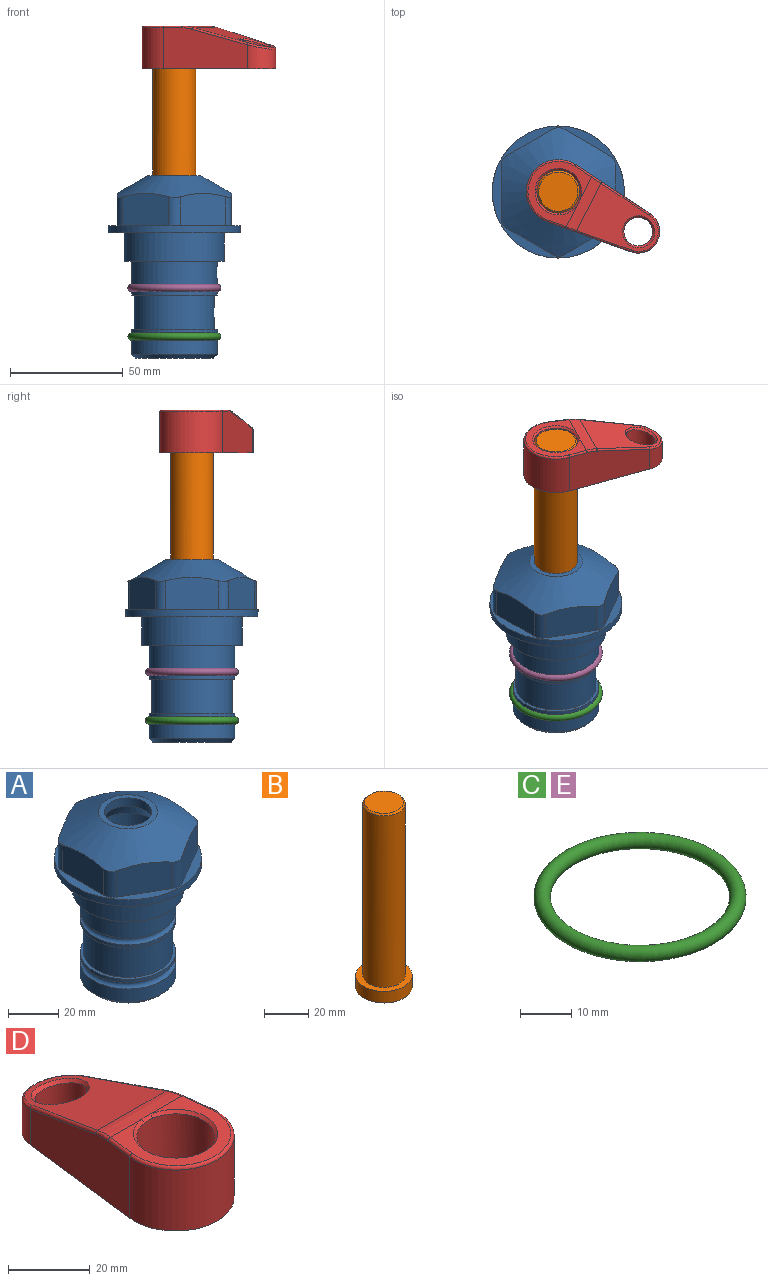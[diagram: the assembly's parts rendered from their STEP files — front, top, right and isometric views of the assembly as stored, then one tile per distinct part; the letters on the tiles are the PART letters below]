
ASSEMBLY  parts=5 mates=4
PART A: 36 faces, bbox 58.7x58.7x81 mm
  f0: cylinder r=17.78mm len=35.56mm, axis (0,0,1), area 1670.8mm2, adj f23,f24,f31
  f1: cylinder r=19.05mm len=38.1mm, axis (0,0,1), area 1191.9mm2, adj f26,f27,f30
  f2: plane 58.66x58.66mm, normal (0,0,-1), area 1150.6mm2, adj f3,f28
  f3: cylinder r=29.33mm len=58.66mm, axis (0,0,-1), area 585.1mm2, adj f2,f4
  f4: plane 58.66x58.66mm, normal (0,0,1), area 475.9mm2, adj f3,f5,f6,f7,f8,f9,f10,f11
  f5: plane 20.32x14.34mm, normal (-0.5,0.87,0), area 324.4mm2, adj f4,f15,f16,f17
  f6: plane 20.32x14.34mm, normal (0.5,0.87,0), area 324.4mm2, adj f4,f14,f15,f17
  f7: plane 23.48x14.34mm, normal (1,0,0), area 324.4mm2, adj f4,f13,f14,f17
  f8: plane 20.32x14.34mm, normal (0.5,-0.87,0), area 324.4mm2, adj f4,f12,f13,f17
  f9: plane 20.32x14.34mm, normal (-0.5,-0.87,0), area 324.4mm2, adj f4,f11,f12,f17
  f10: plane 23.48x14.34mm, normal (-1,0,0), area 324.4mm2, adj f4,f11,f16,f17
  f11: cylinder r=5.08mm len=12.85mm, axis (0,0,-1), area 67.2mm2, adj f4,f9,f10,f17
  f12: cylinder r=5.08mm len=12.85mm, axis (0,0,-1), area 67.2mm2, adj f4,f8,f9,f17
  f13: cylinder r=5.08mm len=12.85mm, axis (0,0,-1), area 67.2mm2, adj f4,f7,f8,f17
  f14: cylinder r=5.08mm len=12.85mm, axis (0,0,-1), area 67.2mm2, adj f4,f6,f7,f17
  f15: cylinder r=5.08mm len=12.85mm, axis (0,0,-1), area 67.2mm2, adj f4,f5,f6,f17
  f16: cylinder r=5.08mm len=12.85mm, axis (0,0,-1), area 67.2mm2, adj f4,f5,f10,f17
  f17: cone r=11.73mm half-angle=60deg, axis (0,0,-1), area 2071.8mm2, adj f5,f6,f7,f8,f9,f10,f11,f12
  f18: plane 23.46x23.46mm, normal (0,0,1), area 147.4mm2, adj f17,f35
  f19: plane 34.93x34.93mm, normal (0,0,-1), area 958mm2, adj f29
  f20: cylinder r=19.05mm len=38.1mm, axis (0,0,1), area 760.1mm2, adj f21,f29
  f21: torus R=19.05mm, axis (0,0,1), area 565.3mm2, adj f20,f22
  f22: cylinder r=19.05mm len=38.1mm, axis (0,0,1), area 190mm2, adj f21,f23
  f23: plane 38.1x38.1mm, normal (0,0,1), area 146.9mm2, adj f0,f22
  f24: plane 38.1x38.1mm, normal (0,0,-1), area 146.9mm2, adj f0,f25
  f25: cylinder r=19.05mm len=38.1mm, axis (0,0,1), area 190mm2, adj f24,f26
  f26: torus R=19.05mm, axis (0,0,1), area 565.3mm2, adj f1,f25
  f27: plane 44.45x44.45mm, normal (0,0,-1), area 411.7mm2, adj f1,f28
  f28: cylinder r=22.23mm len=44.45mm, axis (0,0,1), area 1773.5mm2, adj f2,f27
  f29: cone r=19.05mm half-angle=45deg, axis (0,0,1), area 257.5mm2, adj f19,f20
  f30: cylinder r=3.17mm len=6.75mm, axis (-1,0,0), area 128mm2, adj f1,f33
  f31: cylinder r=3.17mm len=6.35mm, axis (-1,0,0), area 102.5mm2, adj f0,f33
  f32: plane 25.4x25.4mm, normal (0,0,1), area 506.7mm2, adj f33
  f33: cylinder r=12.7mm len=66.42mm, axis (0,0,-1), area 5236.2mm2, adj f30,f31,f32,f34
  f34: cone r=9.53mm half-angle=30deg, axis (0,0,-1), area 443.4mm2, adj f33,f35
  f35: cylinder r=9.53mm len=19.05mm, axis (0,0,-1), area 240.9mm2, adj f18,f34
PART B: 6 faces, bbox 25.4x25.4x101.6 mm
  f0: plane 17.46x17.46mm, normal (0,0,1), area 239.5mm2, adj f5
  f1: plane 25.4x25.4mm, normal (0,0,-1), area 506.7mm2, adj f2
  f2: cylinder r=12.7mm len=25.4mm, axis (0,0,1), area 506.7mm2, adj f1,f3
  f3: plane 25.4x25.4mm, normal (0,0,1), area 221.7mm2, adj f2,f4
  f4: cylinder r=9.53mm len=94.46mm, axis (0,0,1), area 5653mm2, adj f3,f5
  f5: cone r=8.73mm half-angle=45deg, axis (0,0,-1), area 64.4mm2, adj f0,f4
PART C: 1 faces, bbox 44.7x44.7x3.2 mm
  f0: torus R=19.05mm, axis (0,0,1), area 1193.9mm2
PART D: 31 faces, bbox 31.7x65.5x19.8 mm
  f0: plane 39.12x18.26mm, normal (0.99,0.12,0), area 612.2mm2, adj f1,f4,f7,f11,f13,f15
  f1: cylinder r=9.53mm len=18.91mm, axis (0,0,-1), area 296.1mm2, adj f0,f2,f7,f17
  f2: plane 39.12x18.26mm, normal (-0.99,0.12,0), area 612.2mm2, adj f1,f4,f7,f12,f14,f16
  f3: cylinder r=6.35mm len=12.7mm, axis (0,0,-1), area 362.4mm2, adj f7,f18
  f4: cylinder r=14.29mm len=28.58mm, axis (0,0,-1), area 882.2mm2, adj f0,f2,f7,f10
  f5: cylinder r=9.53mm len=19.05mm, axis (0,0,-1), area 1092.6mm2, adj f7,f19,f20
  f6: plane 26.99x23.69mm, normal (0,0,1), area 216.2mm2, adj f9,f10,f11,f12,f19
  f7: plane 63.5x28.58mm, normal (0,0,-1), area 661.8mm2, adj f0,f1,f2,f3,f4,f5,f22,f23
  f8: plane 33.52x23.6mm, normal (0,0.26,0.97), area 486mm2, adj f9,f15,f16,f17,f18
  f9: cylinder r=19.05mm len=24.72mm, axis (1,0,0), area 120.4mm2, adj f6,f8,f13,f14,f20
  f10: torus R=13.49mm, axis (0,0,1), area 59mm2, adj f4,f6,f11,f12
  f11: cylinder r=0.79mm len=8.67mm, axis (0.12,-0.99,0), area 10.8mm2, adj f0,f6,f10,f13
  f12: cylinder r=0.79mm len=8.67mm, axis (0.12,0.99,0), area 10.8mm2, adj f2,f6,f10,f14
  f13: bspline ~4.95x1.42mm, area 6.1mm2, adj f0,f9,f11,f15
  f14: bspline ~4.95x1.42mm, area 6.1mm2, adj f2,f9,f12,f16
  f15: cylinder r=0.79mm len=25.95mm, axis (0.12,-0.96,0.26), area 32.9mm2, adj f0,f8,f13,f17
  f16: cylinder r=0.79mm len=25.95mm, axis (0.12,0.96,-0.26), area 32.9mm2, adj f2,f8,f14,f17
  f17: bspline ~18.91x8.38mm, area 30mm2, adj f1,f8,f15,f16
  f18: bspline ~14.29x14.29mm, area 48.3mm2, adj f3,f8
  f19: cone r=9.53mm half-angle=45deg, axis (0,0,1), area 66.5mm2, adj f5,f6,f20
  f20: bspline ~3.22x0.96mm, area 3.5mm2, adj f5,f9,f19
  f21: plane 2.75x2.72mm, normal (0,0,-1), area 2.9mm2, adj f23,f25,f28
  f22: plane 23.05x15.88mm, normal (-0.99,-0.12,0), area 323.6mm2, adj f7,f25,f26,f27,f28,f29
  f23: plane 23.05x15.88mm, normal (0.99,-0.12,0), area 323.6mm2, adj f7,f21,f25,f27,f28,f30
  f24: cylinder r=9.53mm len=10.69mm, axis (0,0,-1), area 114.7mm2, adj f7,f27,f29,f30
  f25: cylinder r=12.7mm len=20.59mm, axis (0,0,-1), area 381.1mm2, adj f7,f21,f22,f23,f26,f28
  f26: plane 2.75x2.72mm, normal (0,0,-1), area 2.9mm2, adj f22,f25,f28
  f27: plane 19.72x18.37mm, normal (0,-0.26,-0.97), area 291.8mm2, adj f22,f23,f24,f28,f29,f30
  f28: cylinder r=15.88mm len=19.92mm, axis (1,0,0), area 54.8mm2, adj f21,f22,f23,f25,f26,f27
  f29: cylinder r=1.59mm len=11mm, axis (0,0,-1), area 34.7mm2, adj f7,f22,f24,f27
  f30: cylinder r=1.59mm len=11mm, axis (0,0,-1), area 34.7mm2, adj f7,f23,f24,f27
PART E: same geometry as C
PLACE A at identity fixed
PLACE B rot(axis=(0,0,-1),116.6deg) t=(0,0,27.55)mm
PLACE C t=(0,0,-21.59)mm
PLACE D rot(axis=(0,0,-1),116.6deg) t=(0,0,28.35)mm
PLACE E at identity
MATE fastened E.f0 <-> A.f0  axis (0,0,1) through (0,0,-24.51)mm
MATE fastened C.f0 <-> A.f0  axis (0,0,1) through (0,0,-46.1)mm
MATE fastened B.f2 <-> D.f4  axis (0,0,1) through (0,0,91.05)mm
MATE cylindrical B.f2 <-> A.f0  axis (0,0,-1) through (0,0,-10.55)mm
